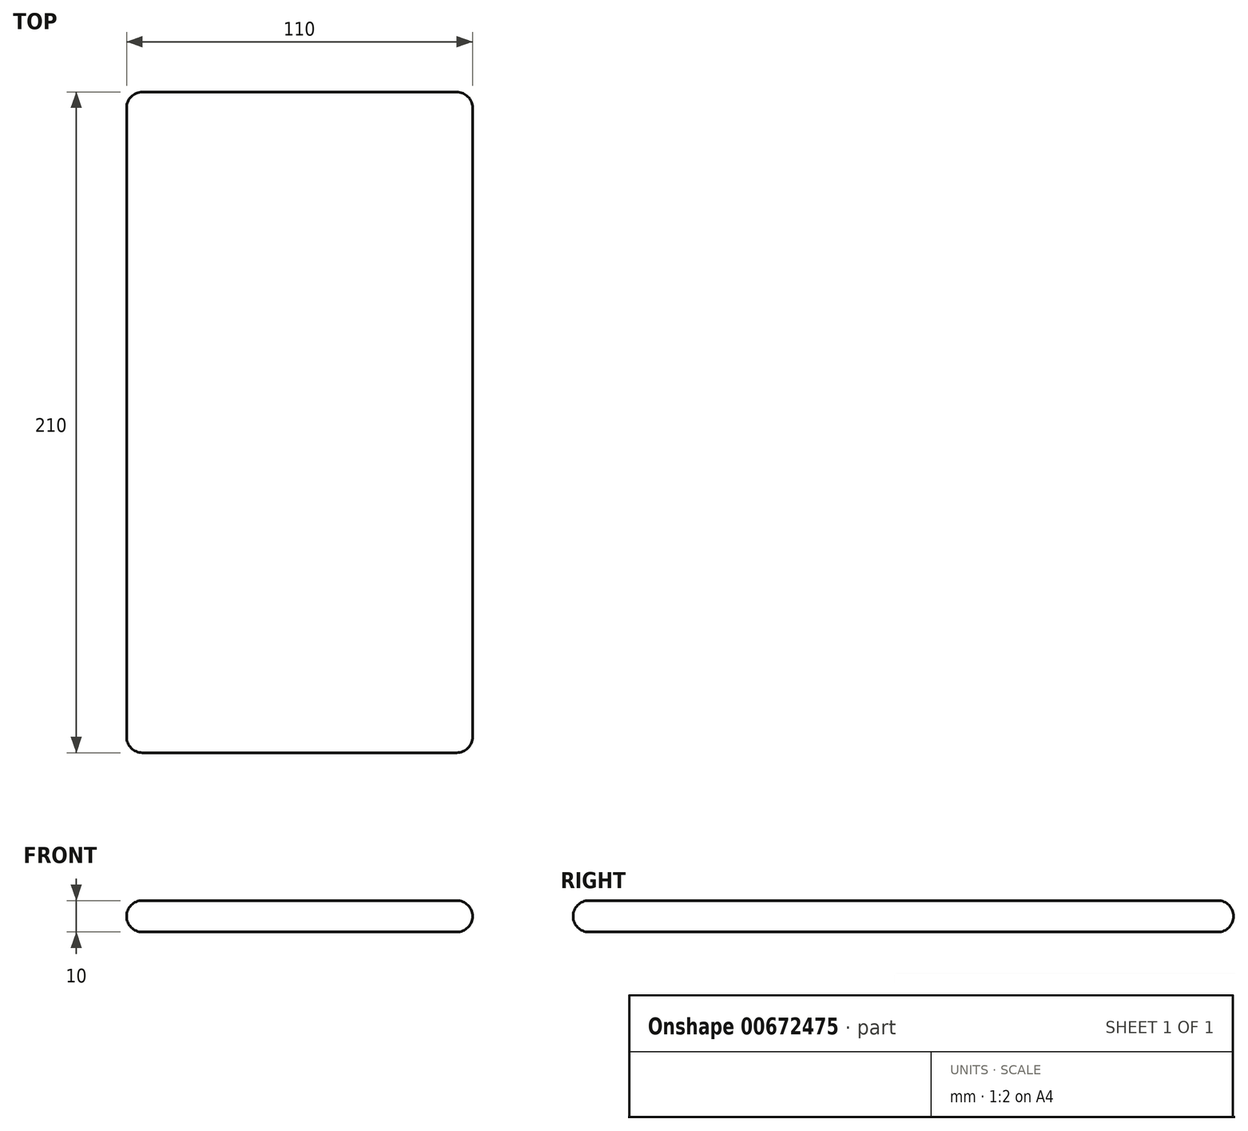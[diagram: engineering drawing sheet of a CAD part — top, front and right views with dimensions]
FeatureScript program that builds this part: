
annotation { "Feature Type Name" : "Feature", "Feature Type Description" : "" }
export const myFeature = defineFeature(function(context is Context, id is Id, definition is map)
    precondition{}
    {
        {
            var Q0;
            Q0=qCreatedBy(makeId("Top.planeOp"),FACE);
            var sketch = newSketch(context, id + "F0", { "sketchPlane" : qUnion([Q0])});
            skLineSegment(sketch, "E0.bottom", {"start": v(55, -105) * mm, "end": v(-55, -105) * mm});
            skLineSegment(sketch, "E0.top", {"start": v(55, 105) * mm, "end": v(-55, 105) * mm});
            skLineSegment(sketch, "E0.left", {"start": v(55, -105) * mm, "end": v(55, 105) * mm});
            skLineSegment(sketch, "E0.right", {"start": v(-55, -105) * mm, "end": v(-55, 105) * mm});
            skPoint(sketch, "E0.middle", {"position": v(0, 0) * mm});
            skSolve(sketch);
        }
        {
            var Q0;
            Q0=qSketchRegion(id+"F0",true);
            extrude(context, id + "F1", {"entities" : qUnion([Q0]), "depth" : 10 * mm, "offsetDistance" : 25 * mm});
        }
        {
            var Q0;
            Q0=makeQuery(id+"F1.opExtrude","CAP_EDGE",EDGE,{"disambiguationData":[OSD([sQuery(id+"F0.wireOp",EDGE,"E0.right")])],"isStart":false});
            var Q1;
            Q1=makeQuery(id+"F1.opExtrude","CAP_EDGE",EDGE,{"disambiguationData":[OSD([sQuery(id+"F0.wireOp",EDGE,"E0.bottom")])],"isStart":false});
            var Q2;
            Q2=makeQuery(id+"F1.opExtrude","CAP_EDGE",EDGE,{"disambiguationData":[OSD([sQuery(id+"F0.wireOp",EDGE,"E0.bottom")])],"isStart":true});
            var Q3;
            Q3=makeQuery(id+"F1.opExtrude","SWEPT_EDGE",EDGE,{"disambiguationData":[OSD([sQuery(id+"F0.wireOp",EDGE,"E0.bottom"),sQuery(id+"F0.wireOp",EDGE,"E0.right")])]});
            var Q4;
            Q4=makeQuery(id+"F1.opExtrude","CAP_EDGE",EDGE,{"disambiguationData":[OSD([sQuery(id+"F0.wireOp",EDGE,"E0.right")])],"isStart":true});
            var Q5;
            Q5=makeQuery(id+"F1.opExtrude","SWEPT_EDGE",EDGE,{"disambiguationData":[OSD([sQuery(id+"F0.wireOp",EDGE,"E0.top"),sQuery(id+"F0.wireOp",EDGE,"E0.right")])]});
            var Q6;
            Q6=makeQuery(id+"F1.opExtrude","CAP_EDGE",EDGE,{"disambiguationData":[OSD([sQuery(id+"F0.wireOp",EDGE,"E0.top")])],"isStart":false});
            var Q7;
            Q7=makeQuery(id+"F1.opExtrude","CAP_EDGE",EDGE,{"disambiguationData":[OSD([sQuery(id+"F0.wireOp",EDGE,"E0.top")])],"isStart":true});
            var Q8;
            Q8=makeQuery(id+"F1.opExtrude","SWEPT_EDGE",EDGE,{"disambiguationData":[OSD([sQuery(id+"F0.wireOp",EDGE,"E0.top"),sQuery(id+"F0.wireOp",EDGE,"E0.left")])]});
            var Q9;
            Q9=makeQuery(id+"F1.opExtrude","CAP_EDGE",EDGE,{"disambiguationData":[OSD([sQuery(id+"F0.wireOp",EDGE,"E0.left")])],"isStart":false});
            var Q10;
            Q10=makeQuery(id+"F1.opExtrude","CAP_EDGE",EDGE,{"disambiguationData":[OSD([sQuery(id+"F0.wireOp",EDGE,"E0.left")])],"isStart":true});
            var Q11;
            Q11=makeQuery(id+"F1.opExtrude","SWEPT_EDGE",EDGE,{"disambiguationData":[OSD([sQuery(id+"F0.wireOp",EDGE,"E0.bottom"),sQuery(id+"F0.wireOp",EDGE,"E0.left")])]});
            fillet(context, id + "F2", {"entities" : qUnion([Q0, Q1, Q2, Q3, Q4, Q5, Q6, Q7, Q8, Q9, Q10, Q11]), "radius" : 5 * mm, "tangentPropagation" : true, "allowEdgeOverflow" : false});
        }
    });
